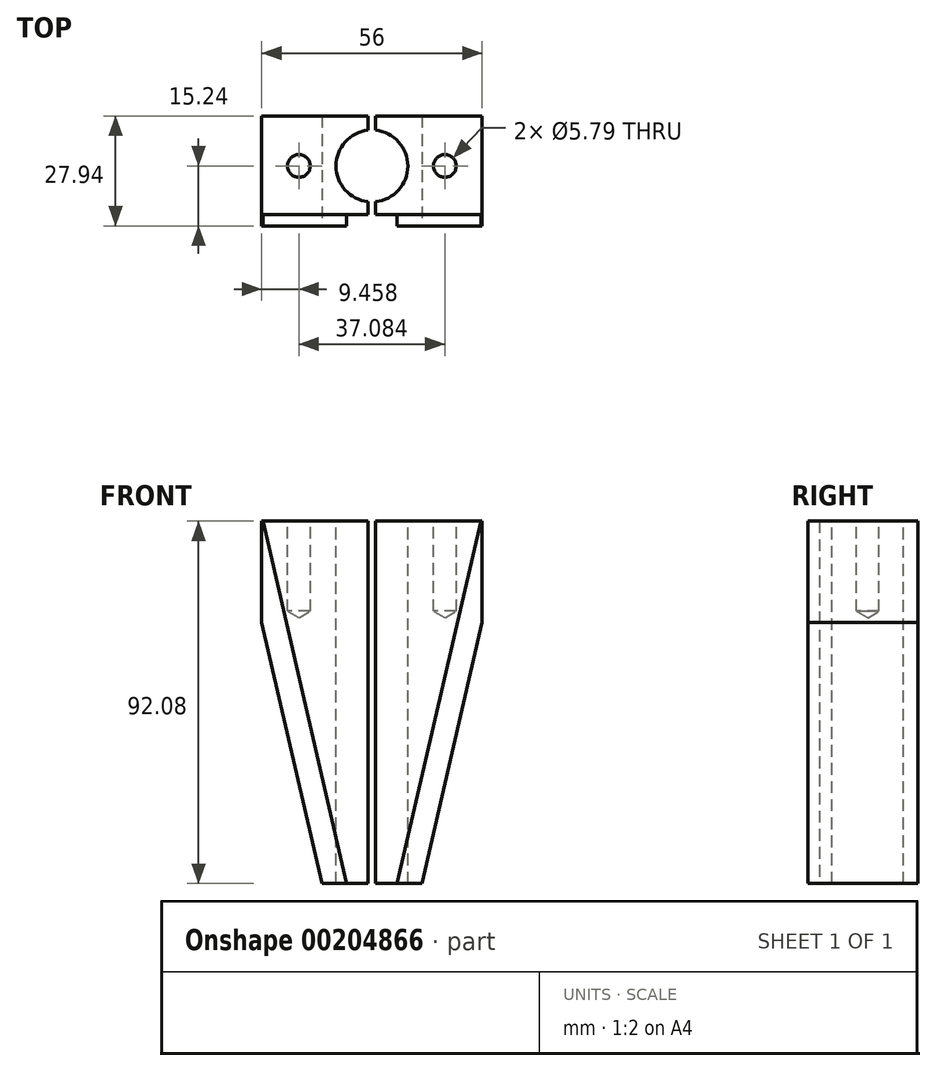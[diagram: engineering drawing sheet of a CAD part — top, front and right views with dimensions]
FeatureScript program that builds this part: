
annotation { "Feature Type Name" : "Feature", "Feature Type Description" : "" }
export const myFeature = defineFeature(function(context is Context, id is Id, definition is map)
    precondition{}
    {
        {
            var Q0;
            Q0=qCreatedBy(makeId("Front.planeOp"),FACE);
            var sketch = newSketch(context, id + "F0", { "sketchPlane" : qUnion([Q0])});
            skLineSegment(sketch, "E0", {"start": v(-28, 0) * mm, "end": v(28, 0) * mm});
            skLineSegment(sketch, "E1", {"start": v(28, 0) * mm, "end": v(28, -25.79) * mm});
            skLineSegment(sketch, "E2", {"start": v(28, -25.79) * mm, "end": v(12.7, -92.08) * mm});
            skLineSegment(sketch, "E3", {"start": v(12.7, -92.08) * mm, "end": v(-12.7, -92.08) * mm});
            skLineSegment(sketch, "E4", {"start": v(-12.7, -92.07) * mm, "end": v(-28, -25.79) * mm});
            skLineSegment(sketch, "E5", {"start": v(-28, -25.79) * mm, "end": v(-28, 0) * mm});
            skLineSegment(sketch, "E6", {"start": v(0, 0) * mm, "end": v(0, -92.08) * mm, "construction": true});
            skSolve(sketch);
        }
        {
            var Q0;
            Q0=makeQuery(id+"F0.imprint","IMPRINT",FACE,{"disambiguationData":[TD([[makeQuery(id+"F0.imprint","IMPRINT",EDGE,{"derivedFrom":sQuery(id+"F0.wireOp",EDGE,"E0")}),-1.0]])]});
            extrude(context, id + "F1", {"entities" : qUnion([Q0]), "oppositeDirection" : true, "depth" : 27.94 * mm});
        }
        {
            var Q0;
            Q0=makeQuery(id+"F1.opExtrude","CAP_FACE",FACE,{"disambiguationData":[OSD([sQuery(id+"F0.wireOp",EDGE,"E0"),sQuery(id+"F0.wireOp",EDGE,"E1"),sQuery(id+"F0.wireOp",EDGE,"E2"),sQuery(id+"F0.wireOp",EDGE,"E3"),sQuery(id+"F0.wireOp",EDGE,"E4"),sQuery(id+"F0.wireOp",EDGE,"E5")])],"isStart":true});
            var sketch = newSketch(context, id + "F2", { "sketchPlane" : qUnion([Q0])});
            skLineSegment(sketch, "E7", {"start": v(-6.44, -92.08) * mm, "end": v(-27.7, 0) * mm});
            skLineSegment(sketch, "E8", {"start": v(6.44, -92.08) * mm, "end": v(27.7, 0) * mm});
            skLineSegment(sketch, "E9", {"start": v(27.7, 0) * mm, "end": v(-27.7, 0) * mm});
            skLineSegment(sketch, "E10", {"start": v(-6.44, -92.08) * mm, "end": v(6.44, -92.07) * mm});
            skSolve(sketch);
        }
        {
            var Q0;
            Q0=makeQuery(id+"F2.imprint","IMPRINT",FACE,{"disambiguationData":[TD([[makeQuery(id+"F2.imprint","IMPRINT",EDGE,{"derivedFrom":sQuery(id+"F2.wireOp",EDGE,"E7")}),-1.0]])]});
            extrude(context, id + "F3", {"entities" : qUnion([Q0]), "operationType" : NewBodyOperationType.REMOVE, "oppositeDirection" : true, "depth" : 2.92 * mm});
        }
        {
            var Q0;
            Q0=makeQuery(id+"F1.opExtrude","SWEPT_FACE",FACE,{"disambiguationData":[OSD([sQuery(id+"F0.wireOp",EDGE,"E0")])]});
            var sketch = newSketch(context, id + "F4", { "sketchPlane" : qUnion([Q0])});
            skCircle(sketch, "E11", {"center": v(-18.54, 15.24) * mm, "radius": 2.7 * mm});
            skCircle(sketch, "E12", {"center": v(18.54, 15.24) * mm, "radius": 2.7 * mm});
            skSolve(sketch);
        }
        {
            var Q0;
            Q0=sQuery(id+"F4.wireOp",VERTEX,"E11.center");
            var Q1;
            Q1=sQuery(id+"F4.wireOp",VERTEX,"E12.center");
            var Q2;
            Q2=makeQuery(id+"F1.opExtrude","SWEPT_BODY",BODY,{"disambiguationData":[OSD([sQuery(id+"F0.wireOp",EDGE,"E0"),sQuery(id+"F0.wireOp",EDGE,"E1"),sQuery(id+"F0.wireOp",EDGE,"E2"),sQuery(id+"F0.wireOp",EDGE,"E3"),sQuery(id+"F0.wireOp",EDGE,"E4"),sQuery(id+"F0.wireOp",EDGE,"E5")])]});
            hole(context, id + "F5", {"style" : HoleStyle.SIMPLE, "endStyle" : HoleEndStyle.BLIND, "standardTappedOrClearance" : lookupTablePath({ "standard" : "ANSI", "engagement" : "50%", "pitch" : "28 tpi", "size" : "1/4", "type" : "Tapped" }), "standardBlindInLast" : lookupTablePath({ "standard" : "ANSI", "engagement" : "50%", "pitch" : "28 tpi", "size" : "1/4", "type" : "Tapped" }), "holeDiameter" : 5.8 * mm, "holeDepth" : 22.86 * mm, "locations" : qUnion([Q0, Q1]), "scope" : qUnion([Q2]), "majorDiameter" : 6.35 * mm});
        }
        {
            var Q0;
            Q0=makeQuery(id+"F1.opExtrude","SWEPT_FACE",FACE,{"disambiguationData":[OSD([sQuery(id+"F0.wireOp",EDGE,"E0")])]});
            var sketch = newSketch(context, id + "F6", { "sketchPlane" : qUnion([Q0])});
            skCircle(sketch, "E13", {"center": v(0, 15.24) * mm, "radius": 9.13 * mm});
            skSolve(sketch);
        }
        {
            var Q0;
            Q0=sQuery(id+"F6.wireOp",VERTEX,"E13.center");
            var Q1;
            Q1=makeQuery(id+"F1.opExtrude","SWEPT_BODY",BODY,{"disambiguationData":[OSD([sQuery(id+"F0.wireOp",EDGE,"E0"),sQuery(id+"F0.wireOp",EDGE,"E1"),sQuery(id+"F0.wireOp",EDGE,"E2"),sQuery(id+"F0.wireOp",EDGE,"E3"),sQuery(id+"F0.wireOp",EDGE,"E4"),sQuery(id+"F0.wireOp",EDGE,"E5")])]});
            hole(context, id + "F7", {"style" : HoleStyle.SIMPLE, "endStyle" : HoleEndStyle.THROUGH, "standardTappedOrClearance" : lookupTablePath({ "standard" : "ANSI", "engagement" : "50%", "pitch" : "20 tpi", "size" : "3/4", "type" : "Tapped" }), "standardBlindInLast" : lookupTablePath({ "standard" : "ANSI", "engagement" : "50%", "pitch" : "20 tpi", "size" : "3/4", "type" : "Tapped" }), "holeDiameter" : 18.26 * mm, "locations" : qUnion([Q0]), "scope" : qUnion([Q1]), "isTappedThrough" : true, "majorDiameter" : 19.05 * mm, "showTappedDepth" : true});
        }
        {
            var Q0;
            Q0=makeQuery(id+"F3.boolean.opBoolean","COPY",FACE,{"derivedFrom":makeQuery(id+"F3.opExtrude","CAP_FACE",FACE,{"disambiguationData":[OSD([sQuery(id+"F2.wireOp",EDGE,"E7"),sQuery(id+"F2.wireOp",EDGE,"E8"),sQuery(id+"F2.wireOp",EDGE,"E9"),sQuery(id+"F2.wireOp",EDGE,"E10")])],"isStart":false})});
            var sketch = newSketch(context, id + "F8", { "sketchPlane" : qUnion([Q0])});
            skLineSegment(sketch, "E14.bottom", {"start": v(-0.95, 0) * mm, "end": v(0.95, 0) * mm});
            skLineSegment(sketch, "E14.top", {"start": v(-0.95, -92.08) * mm, "end": v(0.95, -92.08) * mm});
            skLineSegment(sketch, "E14.left", {"start": v(-0.95, 0) * mm, "end": v(-0.95, -92.08) * mm});
            skLineSegment(sketch, "E14.right", {"start": v(0.95, 0) * mm, "end": v(0.95, -92.08) * mm});
            skSolve(sketch);
        }
        {
            var Q0;
            Q0=makeQuery(id+"F8.imprint","IMPRINT",FACE,{"disambiguationData":[TD([[makeQuery(id+"F8.imprint","IMPRINT",EDGE,{"derivedFrom":sQuery(id+"F8.wireOp",EDGE,"E14.bottom")}),-1.0]])]});
            extrude(context, id + "F9", {"entities" : qUnion([Q0]), "operationType" : NewBodyOperationType.REMOVE, "endBound" : BoundingType.THROUGH_ALL, "oppositeDirection" : true, "depth" : 25.4 * mm});
        }
    });
